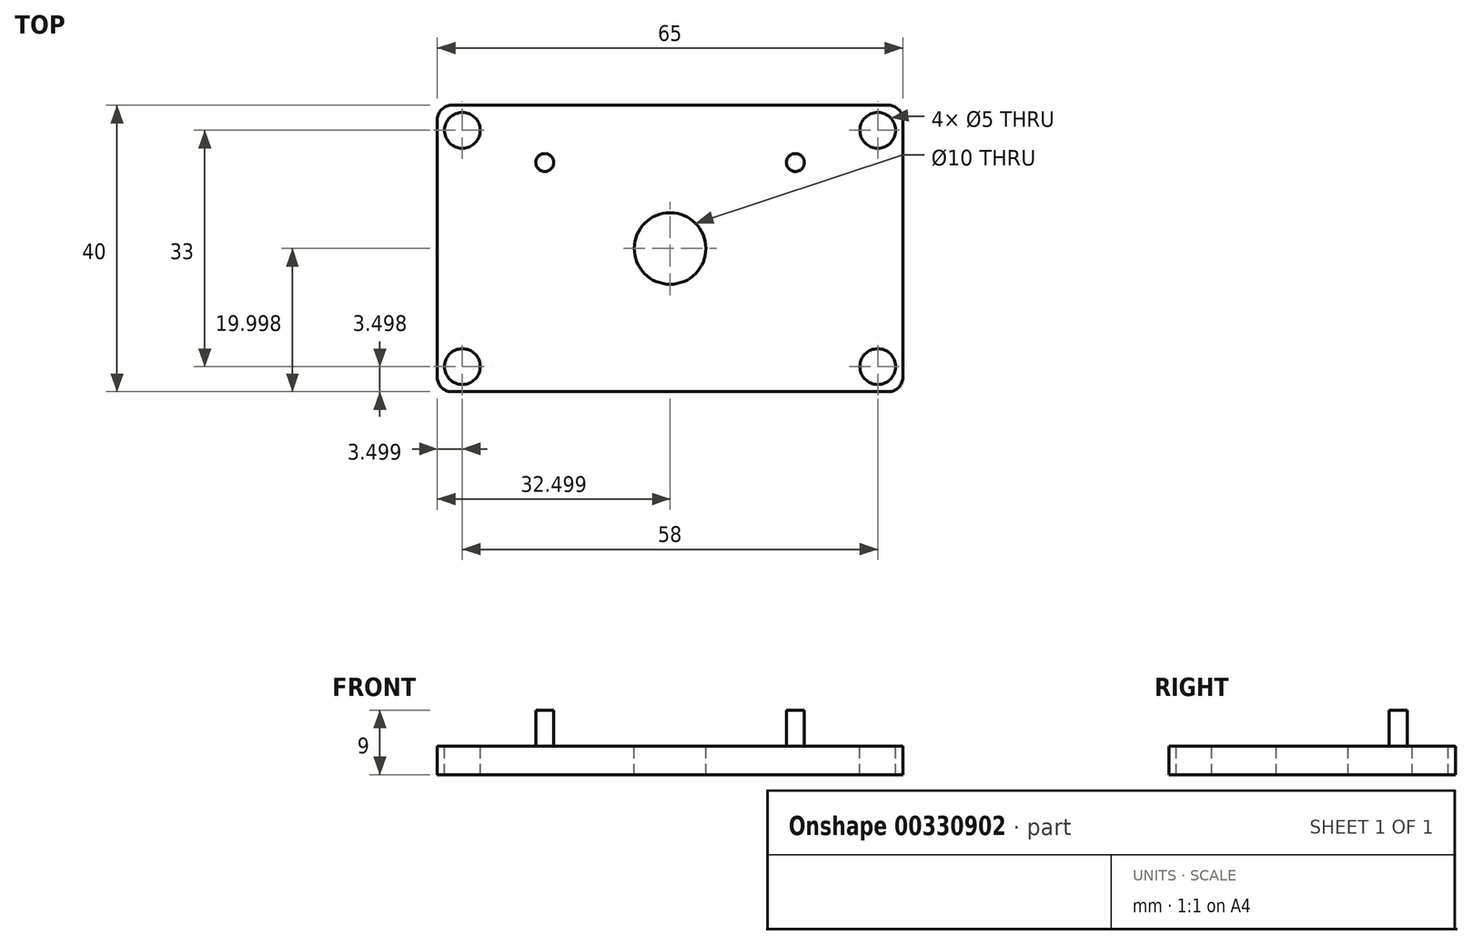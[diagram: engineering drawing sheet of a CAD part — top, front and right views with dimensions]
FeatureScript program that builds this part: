
annotation { "Feature Type Name" : "Feature", "Feature Type Description" : "" }
export const myFeature = defineFeature(function(context is Context, id is Id, definition is map)
    precondition{}
    {
        {
            var Q0;
            Q0=qCreatedBy(makeId("Top.planeOp"),FACE);
            var sketch = newSketch(context, id + "F0", { "sketchPlane" : qUnion([Q0])});
            skLineSegment(sketch, "E0.bottom", {"start": v(0.14, 0.22) * mm, "end": v(65.14, 0.22) * mm});
            skLineSegment(sketch, "E0.top", {"start": v(0.14, 40.22) * mm, "end": v(65.14, 40.22) * mm});
            skLineSegment(sketch, "E0.left", {"start": v(0.14, 0.22) * mm, "end": v(0.14, 40.22) * mm});
            skLineSegment(sketch, "E0.right", {"start": v(65.14, 0.22) * mm, "end": v(65.14, 40.22) * mm});
            skSolve(sketch);
        }
        {
            var Q0;
            Q0=makeQuery(id+"F0.imprint","IMPRINT",FACE,{"disambiguationData":[TD([[makeQuery(id+"F0.imprint","IMPRINT",EDGE,{"derivedFrom":sQuery(id+"F0.wireOp",EDGE,"E0.bottom")}),1.0]])]});
            extrude(context, id + "F1", {"entities" : qUnion([Q0]), "depth" : 4 * mm});
        }
        {
            var Q0;
            Q0=makeQuery(id+"F1.opExtrude","CAP_FACE",FACE,{"disambiguationData":[OSD([sQuery(id+"F0.wireOp",EDGE,"E0.bottom"),sQuery(id+"F0.wireOp",EDGE,"E0.top"),sQuery(id+"F0.wireOp",EDGE,"E0.left"),sQuery(id+"F0.wireOp",EDGE,"E0.right")])],"isStart":false});
            var sketch = newSketch(context, id + "F2", { "sketchPlane" : qUnion([Q0])});
            skPoint(sketch, "E1.startSnap0", {"position": v(65.14, 20.22) * mm});
            skPoint(sketch, "E1.startSnap1", {"position": v(32.64, 0.22) * mm});
            skCircle(sketch, "E2", {"center": v(32.64, 20.22) * mm, "radius": 5 * mm});
            skCircle(sketch, "E3", {"center": v(15.14, 32.22) * mm, "radius": 1.25 * mm});
            skCircle(sketch, "E4", {"center": v(50.14, 32.22) * mm, "radius": 1.25 * mm});
            skSolve(sketch);
        }
        {
            var Q0;
            Q0=makeQuery(id+"F2.imprint","IMPRINT",FACE,{"disambiguationData":[TD([[makeQuery(id+"F2.imprint","IMPRINT",EDGE,{"derivedFrom":sQuery(id+"F2.wireOp",EDGE,"E2")}),1.0]])]});
            extrude(context, id + "F3", {"entities" : qUnion([Q0]), "operationType" : NewBodyOperationType.REMOVE, "oppositeDirection" : true, "depth" : 25 * mm});
        }
        {
            var Q0;
            Q0=makeQuery(id+"F1.opExtrude","CAP_FACE",FACE,{"disambiguationData":[OSD([sQuery(id+"F0.wireOp",EDGE,"E0.bottom"),sQuery(id+"F0.wireOp",EDGE,"E0.top"),sQuery(id+"F0.wireOp",EDGE,"E0.left"),sQuery(id+"F0.wireOp",EDGE,"E0.right")])],"isStart":false});
            var sketch = newSketch(context, id + "F4", { "sketchPlane" : qUnion([Q0])});
            skLineSegment(sketch, "E5", {"start": v(32.64, 20.22) * mm, "end": v(32.64, 32.22) * mm});
            skLineSegment(sketch, "E6", {"start": v(32.64, 32.22) * mm, "end": v(50.14, 32.22) * mm});
            skLineSegment(sketch, "E7", {"start": v(32.64, 32.22) * mm, "end": v(15.14, 32.22) * mm});
            skCircle(sketch, "E8", {"center": v(15.14, 32.22) * mm, "radius": 1.25 * mm});
            skCircle(sketch, "E9", {"center": v(50.14, 32.22) * mm, "radius": 1.25 * mm});
            skSolve(sketch);
        }
        {
            var Q0;
            Q0=makeQuery(id+"F4.imprint","IMPRINT",FACE,{"disambiguationData":[TD([[makeQuery(id+"F4.imprint","IMPRINT",EDGE,{"derivedFrom":sQuery(id+"F4.wireOp",EDGE,"E9")}),1.0]])]});
            var Q1;
            Q1=makeQuery(id+"F4.imprint","IMPRINT",FACE,{"disambiguationData":[TD([[makeQuery(id+"F4.imprint","IMPRINT",EDGE,{"derivedFrom":sQuery(id+"F4.wireOp",EDGE,"E8")}),1.0]])]});
            extrude(context, id + "F5", {"entities" : qUnion([Q0, Q1]), "operationType" : NewBodyOperationType.ADD, "depth" : 5 * mm});
        }
        {
            var Q0;
            Q0=makeQuery(id+"F1.opExtrude","SWEPT_EDGE",EDGE,{"disambiguationData":[OSD([sQuery(id+"F0.wireOp",EDGE,"E0.bottom"),sQuery(id+"F0.wireOp",EDGE,"E0.left")])]});
            var Q1;
            Q1=makeQuery(id+"F1.opExtrude","SWEPT_EDGE",EDGE,{"disambiguationData":[OSD([sQuery(id+"F0.wireOp",EDGE,"E0.bottom"),sQuery(id+"F0.wireOp",EDGE,"E0.right")])]});
            var Q2;
            Q2=makeQuery(id+"F1.opExtrude","SWEPT_EDGE",EDGE,{"disambiguationData":[OSD([sQuery(id+"F0.wireOp",EDGE,"E0.top"),sQuery(id+"F0.wireOp",EDGE,"E0.right")])]});
            var Q3;
            Q3=makeQuery(id+"F1.opExtrude","SWEPT_EDGE",EDGE,{"disambiguationData":[OSD([sQuery(id+"F0.wireOp",EDGE,"E0.top"),sQuery(id+"F0.wireOp",EDGE,"E0.left")])]});
            fillet(context, id + "F6", {"entities" : qUnion([Q0, Q1, Q2, Q3]), "radius" : 2 * mm, "tangentPropagation" : true, "allowEdgeOverflow" : false});
        }
        {
            var Q0;
            Q0=makeQuery(id+"F1.opExtrude","CAP_FACE",FACE,{"disambiguationData":[OSD([sQuery(id+"F0.wireOp",EDGE,"E0.bottom"),sQuery(id+"F0.wireOp",EDGE,"E0.top"),sQuery(id+"F0.wireOp",EDGE,"E0.left"),sQuery(id+"F0.wireOp",EDGE,"E0.right")])],"isStart":false});
            var sketch = newSketch(context, id + "F7", { "sketchPlane" : qUnion([Q0])});
            skLineSegment(sketch, "E10", {"start": v(32.64, 0.22) * mm, "end": v(32.64, 3.72) * mm});
            skLineSegment(sketch, "E11", {"start": v(32.64, 3.72) * mm, "end": v(61.64, 3.72) * mm});
            skCircle(sketch, "E12", {"center": v(61.64, 3.72) * mm, "radius": 2.5 * mm});
            skLineSegment(sketch, "E13", {"start": v(32.64, 3.72) * mm, "end": v(3.64, 3.72) * mm});
            skCircle(sketch, "E14", {"center": v(3.64, 3.72) * mm, "radius": 2.5 * mm});
            skLineSegment(sketch, "E15", {"start": v(32.64, 40.22) * mm, "end": v(32.64, 36.72) * mm});
            skLineSegment(sketch, "E16", {"start": v(32.64, 36.72) * mm, "end": v(61.64, 36.72) * mm});
            skLineSegment(sketch, "E17", {"start": v(32.64, 36.72) * mm, "end": v(3.64, 36.72) * mm});
            skCircle(sketch, "E18", {"center": v(3.64, 36.72) * mm, "radius": 2.5 * mm});
            skCircle(sketch, "E19", {"center": v(61.64, 36.72) * mm, "radius": 2.5 * mm});
            skSolve(sketch);
        }
        {
            var Q0;
            Q0=makeQuery(id+"F7.imprint","IMPRINT",FACE,{"disambiguationData":[TD([[makeQuery(id+"F7.imprint","IMPRINT",EDGE,{"derivedFrom":sQuery(id+"F7.wireOp",EDGE,"E18")}),1.0]])]});
            var Q1;
            Q1=makeQuery(id+"F7.imprint","IMPRINT",FACE,{"disambiguationData":[TD([[makeQuery(id+"F7.imprint","IMPRINT",EDGE,{"derivedFrom":sQuery(id+"F7.wireOp",EDGE,"E14")}),1.0]])]});
            var Q2;
            Q2=makeQuery(id+"F7.imprint","IMPRINT",FACE,{"disambiguationData":[TD([[makeQuery(id+"F7.imprint","IMPRINT",EDGE,{"derivedFrom":sQuery(id+"F7.wireOp",EDGE,"E12")}),1.0]])]});
            var Q3;
            Q3=makeQuery(id+"F7.imprint","IMPRINT",FACE,{"disambiguationData":[TD([[makeQuery(id+"F7.imprint","IMPRINT",EDGE,{"derivedFrom":sQuery(id+"F7.wireOp",EDGE,"E19")}),1.0]])]});
            extrude(context, id + "F8", {"entities" : qUnion([Q0, Q1, Q2, Q3]), "operationType" : NewBodyOperationType.REMOVE, "oppositeDirection" : true, "depth" : 25 * mm});
        }
    });
